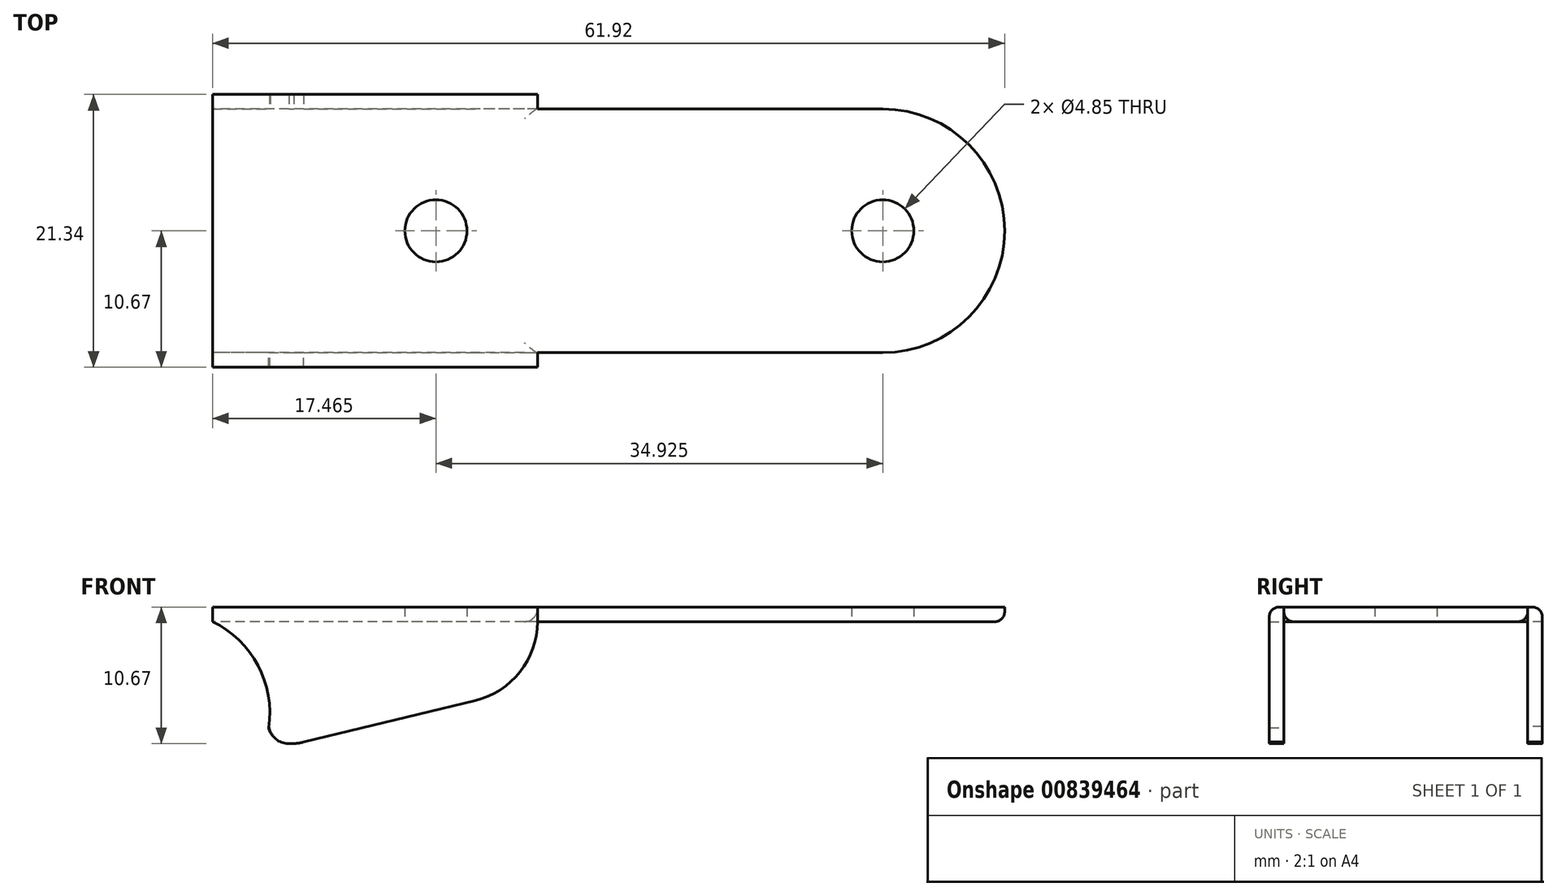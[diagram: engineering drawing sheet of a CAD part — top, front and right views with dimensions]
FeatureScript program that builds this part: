
annotation { "Feature Type Name" : "Feature", "Feature Type Description" : "" }
export const myFeature = defineFeature(function(context is Context, id is Id, definition is map)
    precondition{}
    {
        {
            var Q0;
            Q0=qCreatedBy(makeId("Top.planeOp"),FACE);
            var sketch = newSketch(context, id + "F0", { "sketchPlane" : qUnion([Q0])});
            skCircle(sketch, "E0", {"center": v(0, 0) * mm, "radius": 2.43 * mm});
            skCircle(sketch, "E1", {"center": v(-34.93, 0) * mm, "radius": 2.43 * mm});
            skArc(sketch, "E2", {"start": v(0, -9.53) * mm, "mid": v(9.53, 0) * mm, "end": v(0, 9.53) * mm});
            skLineSegment(sketch, "E3.bottom", {"start": v(0, 9.53) * mm, "end": v(-52.39, 9.52) * mm});
            skLineSegment(sketch, "E3.top", {"start": v(0, -9.53) * mm, "end": v(-52.39, -9.53) * mm});
            skLineSegment(sketch, "E3.right", {"start": v(-52.39, 9.52) * mm, "end": v(-52.39, -9.53) * mm});
            skSolve(sketch);
        }
        {
            var Q0;
            Q0=makeQuery(id+"F0.imprint","IMPRINT",FACE,{"disambiguationData":[TD([[makeQuery(id+"F0.imprint","IMPRINT",EDGE,{"derivedFrom":sQuery(id+"F0.wireOp",EDGE,"E0")}),-1.0]])]});
            extrude(context, id + "F1", {"entities" : qUnion([Q0]), "depth" : 1.14 * mm, "offsetDistance" : 25.4 * mm});
        }
        {
            var Q0;
            Q0=makeQuery(id+"F1.opExtrude","SWEPT_FACE",FACE,{"disambiguationData":[OSD([sQuery(id+"F0.wireOp",EDGE,"E3.top")])]});
            var sketch = newSketch(context, id + "F2", { "sketchPlane" : qUnion([Q0])});
            skLineSegment(sketch, "E4.top", {"start": v(-46.45, -9.53) * mm, "end": v(-46.08, -9.53) * mm});
            skArc(sketch, "E5", {"start": v(-31.84, -6.17) * mm, "mid": v(-28.35, -3.93) * mm, "end": v(-26.99, 0) * mm});
            skPoint(sketch, "E6.visualSharp", {"position": v(-45.66, -9.53) * mm});
            skArc(sketch, "E6.filletArc", {"start": v(-46.08, -9.53) * mm, "mid": v(-45.66, -9.5) * mm, "end": v(-45.26, -9.42) * mm});
            skPoint(sketch, "E7.visualSharp", {"position": v(-47.74, -9.52) * mm});
            skArc(sketch, "E7.filletArc", {"start": v(-48, -8.31) * mm, "mid": v(-47.43, -9.18) * mm, "end": v(-46.45, -9.52) * mm});
            skLineSegment(sketch, "E8", {"start": v(-45.26, -9.42) * mm, "end": v(-31.84, -6.17) * mm});
            skLineSegment(sketch, "E9", {"start": v(-52.39, 0) * mm, "end": v(-52.39, 1.14) * mm});
            skLineSegment(sketch, "E10", {"start": v(-52.39, 1.14) * mm, "end": v(-26.99, 1.14) * mm});
            skLineSegment(sketch, "E11", {"start": v(-26.99, 1.14) * mm, "end": v(-26.99, 0) * mm});
            skArc(sketch, "E12", {"start": v(-48, -8.31) * mm, "mid": v(-48.83, -3.44) * mm, "end": v(-52.39, 0) * mm});
            skSolve(sketch);
        }
        {
            var Q0;
            Q0=makeQuery(id+"F1.opExtrude","SWEPT_FACE",FACE,{"disambiguationData":[OSD([sQuery(id+"F0.wireOp",EDGE,"E3.bottom")])]});
            var sketch = newSketch(context, id + "F3", { "sketchPlane" : qUnion([Q0])});
            skLineSegment(sketch, "E13.MirrorCS", {"start": v(46.4, -9.52) * mm, "end": v(46.02, -9.52) * mm});
            skArc(sketch, "E14.MirrorCS", {"start": v(46.02, -9.52) * mm, "mid": v(45.64, -9.5) * mm, "end": v(45.26, -9.42) * mm});
            skLineSegment(sketch, "E15.MirrorCS", {"start": v(52.39, 0) * mm, "end": v(52.39, 1.14) * mm});
            skLineSegment(sketch, "E16.MirrorCS", {"start": v(26.99, 1.14) * mm, "end": v(26.99, 0) * mm});
            skArc(sketch, "E17.MirrorCS", {"start": v(47.94, -8.2) * mm, "mid": v(47.41, -9.14) * mm, "end": v(46.4, -9.52) * mm});
            skLineSegment(sketch, "E18.MirrorCS", {"start": v(45.26, -9.42) * mm, "end": v(31.84, -6.17) * mm});
            skPoint(sketch, "E19.MirrorP", {"position": v(81.72, -7.55) * mm});
            skPoint(sketch, "E20.MirrorP", {"position": v(83.8, -7.55) * mm});
            skArc(sketch, "E21.MirrorCS", {"start": v(31.84, -6.17) * mm, "mid": v(28.35, -3.93) * mm, "end": v(26.99, 0) * mm});
            skLineSegment(sketch, "E22.MirrorCS", {"start": v(52.39, 1.14) * mm, "end": v(26.99, 1.14) * mm});
            skArc(sketch, "E23", {"start": v(52.39, 0) * mm, "mid": v(48.83, -3.38) * mm, "end": v(47.94, -8.2) * mm});
            skSolve(sketch);
        }
        {
            var Q0;
            Q0=makeQuery(id+"F2.imprint","IMPRINT",FACE,{"disambiguationData":[TD([[makeQuery(id+"F2.imprint","IMPRINT",EDGE,{"derivedFrom":sQuery(id+"F2.wireOp",EDGE,"E4.top")}),1.0]])]});
            var Q1;
            {var subQ0=sQuery(id+"F2.wireOp",EDGE,"E9");Q1=makeQuery(id+"F2.imprint","IMPRINT",FACE,{"disambiguationData":[TD([[makeQuery(id+"F2.imprint","IMPRINT",EDGE,{"derivedFrom":subQ0}),1.0]])]});}
            extrude(context, id + "F4", {"entities" : qUnion([Q0, Q1]), "operationType" : NewBodyOperationType.ADD, "depth" : 1.14 * mm, "offsetDistance" : 25.4 * mm});
        }
        {
            var Q0;
            Q0=makeQuery(id+"F3.imprint","IMPRINT",FACE,{"disambiguationData":[TD([[makeQuery(id+"F3.imprint","IMPRINT",EDGE,{"derivedFrom":sQuery(id+"F3.wireOp",EDGE,"E13.MirrorCS")}),-1.0]])]});
            var Q1;
            {var subQ0=sQuery(id+"F3.wireOp",EDGE,"E15.MirrorCS");Q1=makeQuery(id+"F3.imprint","IMPRINT",FACE,{"disambiguationData":[TD([[makeQuery(id+"F3.imprint","IMPRINT",EDGE,{"derivedFrom":subQ0}),-1.0]])]});}
            extrude(context, id + "F5", {"entities" : qUnion([Q0, Q1]), "operationType" : NewBodyOperationType.ADD, "depth" : 1.14 * mm, "offsetDistance" : 25.4 * mm});
        }
        {
            var Q0;
            Q0=makeQuery(id+"F4.opExtrude","CAP_EDGE",EDGE,{"disambiguationData":[OSD([sQuery(id+"F2.wireOp",EDGE,"E10")])],"isStart":false});
            var Q1;
            {var subQ0=sQuery(id+"F0.wireOp",EDGE,"E3.top");Q1=makeQuery(id+"F4.boolean.opBoolean","SPLIT",EDGE,{"disambiguationData":[topologyDisambiguationEdgeConnected([makeQuery(id+"F4.opExtrude","CAP_FACE",FACE,{"disambiguationData":[OSD([sQuery(id+"F2.wireOp",EDGE,"E4.top"),sQuery(id+"F2.wireOp",EDGE,"E5"),sQuery(id+"F2.wireOp",EDGE,"aApaTyiN-9W00-p4qg-gUqo-M9D3J4en3kLG"),sQuery(id+"F2.wireOp",EDGE,"E6.filletArc"),sQuery(id+"F2.wireOp",EDGE,"E7.filletArc"),sQuery(id+"F2.wireOp",EDGE,"E8"),sQuery(id+"F2.wireOp",EDGE,"E9"),sQuery(id+"F2.wireOp",EDGE,"E10"),sQuery(id+"F2.wireOp",EDGE,"E11")])],"isStart":true})])],"derivedFrom":makeQuery(id+"F1.opExtrude","CAP_EDGE",EDGE,{"disambiguationData":[OSD([subQ0])],"isStart":true})});}
            var Q2;
            Q2=makeQuery(id+"F5.opExtrude","CAP_EDGE",EDGE,{"disambiguationData":[OSD([sQuery(id+"F3.wireOp",EDGE,"E22.MirrorCS")])],"isStart":false});
            var Q3;
            {var subQ0=sQuery(id+"F0.wireOp",EDGE,"E3.bottom");Q3=makeQuery(id+"F5.boolean.opBoolean","SPLIT",EDGE,{"disambiguationData":[topologyDisambiguationEdgeConnected([makeQuery(id+"F5.opExtrude","CAP_FACE",FACE,{"disambiguationData":[OSD([sQuery(id+"F3.wireOp",EDGE,"E13.MirrorCS"),sQuery(id+"F3.wireOp",EDGE,"E14.MirrorCS"),sQuery(id+"F3.wireOp",EDGE,"E15.MirrorCS"),sQuery(id+"F3.wireOp",EDGE,"E16.MirrorCS"),sQuery(id+"F3.wireOp",EDGE,"E17.MirrorCS"),sQuery(id+"F3.wireOp",EDGE,"E18.MirrorCS"),sQuery(id+"F3.wireOp",EDGE,"9986b27d-b826-4cda-a295-01a849f932e98.MirrorCS"),sQuery(id+"F3.wireOp",EDGE,"E21.MirrorCS"),sQuery(id+"F3.wireOp",EDGE,"E22.MirrorCS")])],"isStart":true})])],"derivedFrom":makeQuery(id+"F1.opExtrude","CAP_EDGE",EDGE,{"disambiguationData":[OSD([subQ0])],"isStart":true})});}
            fillet(context, id + "F6", {"entities" : qUnion([Q0, Q1, Q2, Q3]), "radius" : 0.76 * mm, "tangentPropagation" : true, "allowEdgeOverflow" : false});
        }
        {
            var Q0;
            Q0=makeQuery(id+"F4.opExtrude","CAP_EDGE",EDGE,{"disambiguationData":[OSD([sQuery(id+"F2.wireOp",EDGE,"E11")])],"isStart":true});
            var Q1;
            Q1=makeQuery(id+"F4.opExtrude","SWEPT_EDGE",EDGE,{"disambiguationData":[OSD([sQuery(id+"F0.wireOp",EDGE,"E3.top"),sQuery(id+"F2.wireOp",EDGE,"E5"),sQuery(id+"F2.wireOp",EDGE,"E11")])]});
            var Q2;
            Q2=makeQuery(id+"F6.opFillet","TWEAK_EDGE",EDGE,{"derivedFrom":[makeQuery(id+"F4.opExtrude","CAP_VERTEX",VERTEX,{"disambiguationData":[OSD([sQuery(id+"F0.wireOp",EDGE,"E3.top"),sQuery(id+"F2.wireOp",EDGE,"E5"),sQuery(id+"F2.wireOp",EDGE,"E11")])],"isStart":true})]});
            var Q3;
            Q3=makeQuery(id+"F5.opExtrude","CAP_EDGE",EDGE,{"disambiguationData":[OSD([sQuery(id+"F3.wireOp",EDGE,"E16.MirrorCS")])],"isStart":true});
            var Q4;
            Q4=makeQuery(id+"F5.opExtrude","SWEPT_EDGE",EDGE,{"disambiguationData":[OSD([sQuery(id+"F0.wireOp",EDGE,"E3.bottom"),sQuery(id+"F3.wireOp",EDGE,"E16.MirrorCS"),sQuery(id+"F3.wireOp",EDGE,"E21.MirrorCS")])]});
            var Q5;
            Q5=makeQuery(id+"F6.opFillet","TWEAK_EDGE",EDGE,{"derivedFrom":[makeQuery(id+"F5.opExtrude","CAP_VERTEX",VERTEX,{"disambiguationData":[OSD([sQuery(id+"F0.wireOp",EDGE,"E3.bottom"),sQuery(id+"F3.wireOp",EDGE,"E16.MirrorCS"),sQuery(id+"F3.wireOp",EDGE,"E21.MirrorCS")])],"isStart":true})]});
            fillet(context, id + "F7", {"entities" : qUnion([Q0, Q1, Q2, Q3, Q4, Q5]), "radius" : 1.02 * mm, "tangentPropagation" : true, "allowEdgeOverflow" : false});
        }
    });
